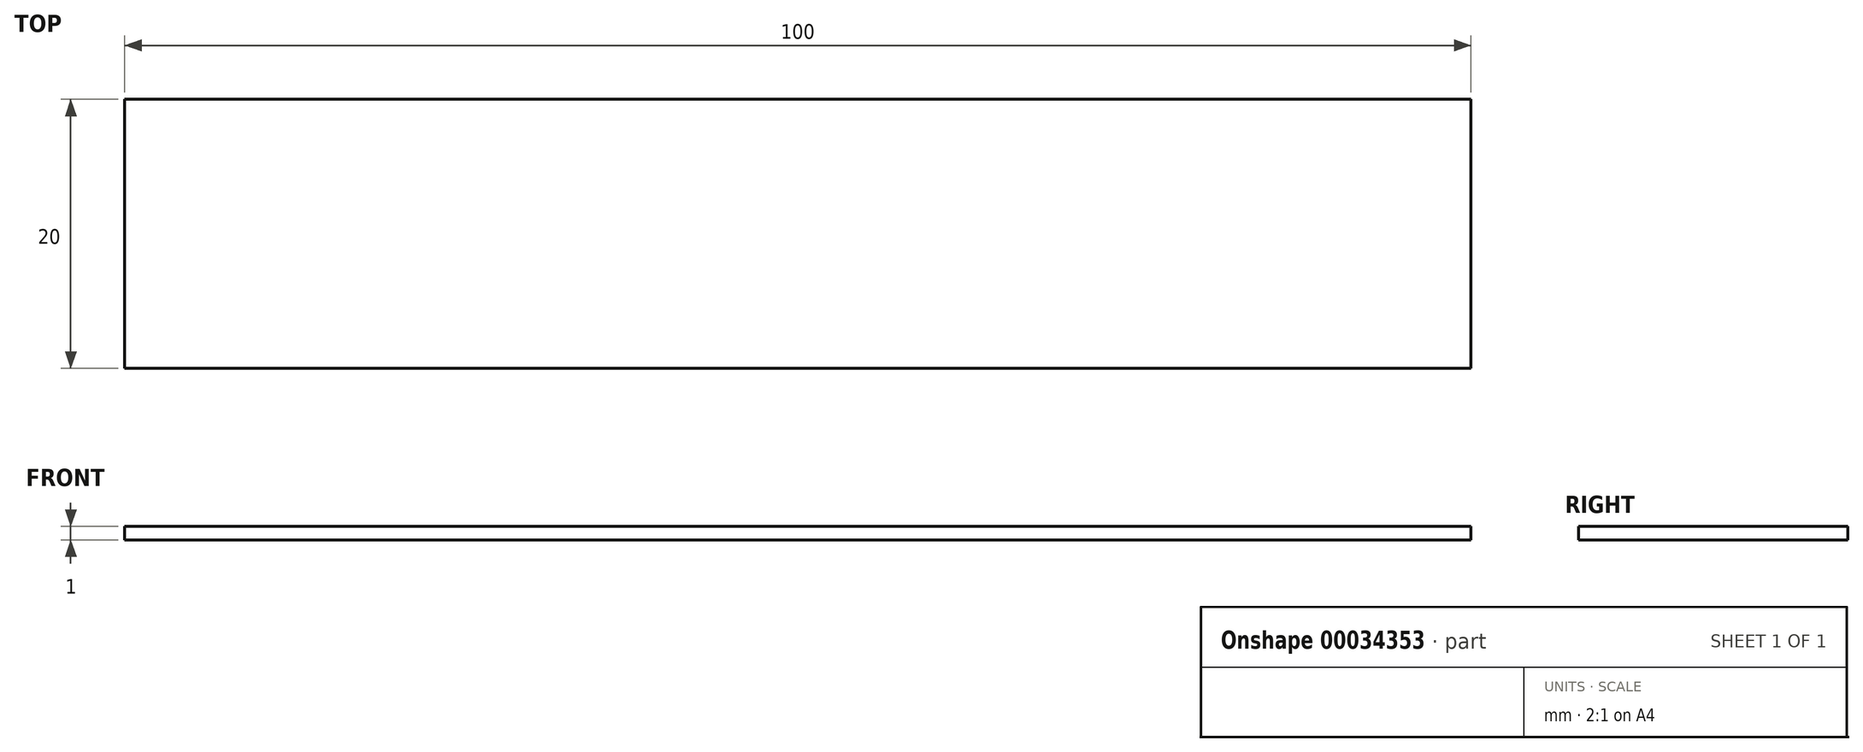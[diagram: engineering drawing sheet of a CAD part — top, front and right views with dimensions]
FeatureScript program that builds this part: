
annotation { "Feature Type Name" : "Feature", "Feature Type Description" : "" }
export const myFeature = defineFeature(function(context is Context, id is Id, definition is map)
    precondition{}
    {
        {
            var Q0;
            Q0=qCreatedBy(makeId("Top.planeOp"),FACE);
            var sketch = newSketch(context, id + "F0", { "sketchPlane" : qUnion([Q0])});
            skLineSegment(sketch, "E0.rect.bottom", {"start": v(50, -10) * mm, "end": v(-50, -10) * mm});
            skLineSegment(sketch, "E0.rect.top", {"start": v(50, 10) * mm, "end": v(-50, 10) * mm});
            skLineSegment(sketch, "E0.rect.left", {"start": v(50, -10) * mm, "end": v(50, 10) * mm});
            skLineSegment(sketch, "E0.rect.right", {"start": v(-50, -10) * mm, "end": v(-50, 10) * mm});
            skPoint(sketch, "E0.rect.middle", {"position": v(0, 0) * mm});
            skSolve(sketch);
        }
        {
            var Q0;
            Q0 = qSketchRegion(id + "F0", true);
            extrude(context, id + "F1", {"entities" : qUnion([Q0]), "depth" : 1 * mm});
        }
    });
